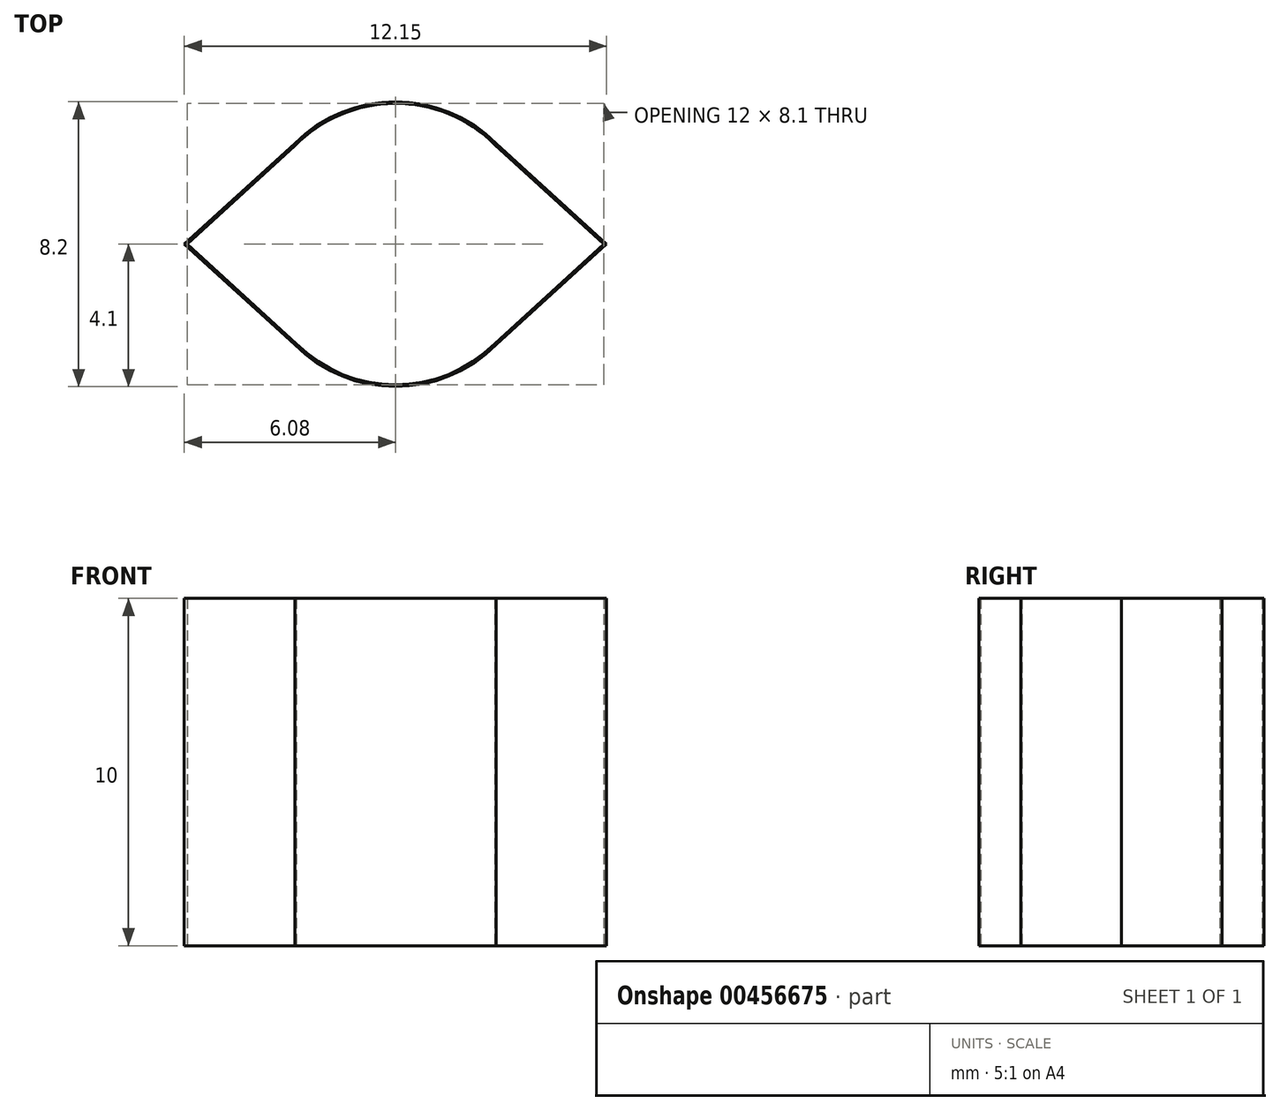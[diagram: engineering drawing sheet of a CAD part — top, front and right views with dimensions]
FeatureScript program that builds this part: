
annotation { "Feature Type Name" : "Feature", "Feature Type Description" : "" }
export const myFeature = defineFeature(function(context is Context, id is Id, definition is map)
    precondition{}
    {
        {
            var Q0;
            Q0=qCreatedBy(makeId("Top.planeOp"),FACE);
            var sketch = newSketch(context, id + "F0", { "sketchPlane" : qUnion([Q0])});
            skArc(sketch, "E0", {"start": v(2.86, 2.86) * mm, "mid": v(-0.02, 4.05) * mm, "end": v(-2.9, 2.83) * mm});
            skLineSegment(sketch, "E1", {"start": v(-6, 4.09) * mm, "end": v(-6, -4.15) * mm, "construction": true});
            skLineSegment(sketch, "E2", {"start": v(6, 4.07) * mm, "end": v(6, -4.11) * mm, "construction": true});
            skArc(sketch, "E3.trimOffspring", {"start": v(-2.86, -2.86) * mm, "mid": v(0, -4.05) * mm, "end": v(2.86, -2.86) * mm});
            skLineSegment(sketch, "E4", {"start": v(2.86, 2.86) * mm, "end": v(6, 0) * mm});
            skLineSegment(sketch, "E5", {"start": v(6, 0) * mm, "end": v(2.86, -2.86) * mm});
            skLineSegment(sketch, "E6", {"start": v(-2.9, 2.83) * mm, "end": v(-6, 0) * mm});
            skLineSegment(sketch, "E7", {"start": v(-6, 0) * mm, "end": v(-2.86, -2.86) * mm});
            skPoint(sketch, "E8.startSnap0", {"position": v(6.1, -0.35) * mm});
            skPoint(sketch, "E9.endSnap0", {"position": v(-2.86, 3.2) * mm});
            skPoint(sketch, "E10.endSnap0", {"position": v(2.86, 0) * mm});
            skArc(sketch, "E11", {"start": v(2.9, 2.9) * mm, "mid": v(0, 4.1) * mm, "end": v(-2.9, 2.9) * mm});
            skLineSegment(sketch, "E12.bottom", {"start": v(-2.9, 2.9) * mm, "end": v(2.9, 2.9) * mm, "construction": true});
            skLineSegment(sketch, "E12.top", {"start": v(-2.9, -2.9) * mm, "end": v(2.9, -2.9) * mm, "construction": true});
            skLineSegment(sketch, "E12.left", {"start": v(-2.9, 2.9) * mm, "end": v(-2.9, -2.9) * mm, "construction": true});
            skLineSegment(sketch, "E12.right", {"start": v(2.9, 2.9) * mm, "end": v(2.9, -2.9) * mm, "construction": true});
            skLineSegment(sketch, "E13", {"start": v(0, 0) * mm, "end": v(-3.9, 3.9) * mm, "construction": true});
            skLineSegment(sketch, "E14", {"start": v(-2.9, 2.9) * mm, "end": v(-6.08, 0) * mm});
            skLineSegment(sketch, "E15", {"start": v(-6.08, 0) * mm, "end": v(-2.9, -2.9) * mm});
            skLineSegment(sketch, "E16", {"start": v(2.9, 2.9) * mm, "end": v(6.07, 0) * mm});
            skLineSegment(sketch, "E17", {"start": v(6.07, 0) * mm, "end": v(2.9, -2.9) * mm});
            skArc(sketch, "E18.trimOffspring", {"start": v(-2.9, -2.9) * mm, "mid": v(0, -4.1) * mm, "end": v(2.9, -2.9) * mm});
            skSolve(sketch);
        }
        {
            var Q0;
            Q0=makeQuery(id+"F0.imprint","IMPRINT",FACE,{"disambiguationData":[TD([[makeQuery(id+"F0.imprint","IMPRINT",EDGE,{"derivedFrom":sQuery(id+"F0.wireOp",EDGE,"E0")}),-1.0]])]});
            extrude(context, id + "F1", {"entities" : qUnion([Q0]), "depth" : 10 * mm});
        }
    });
